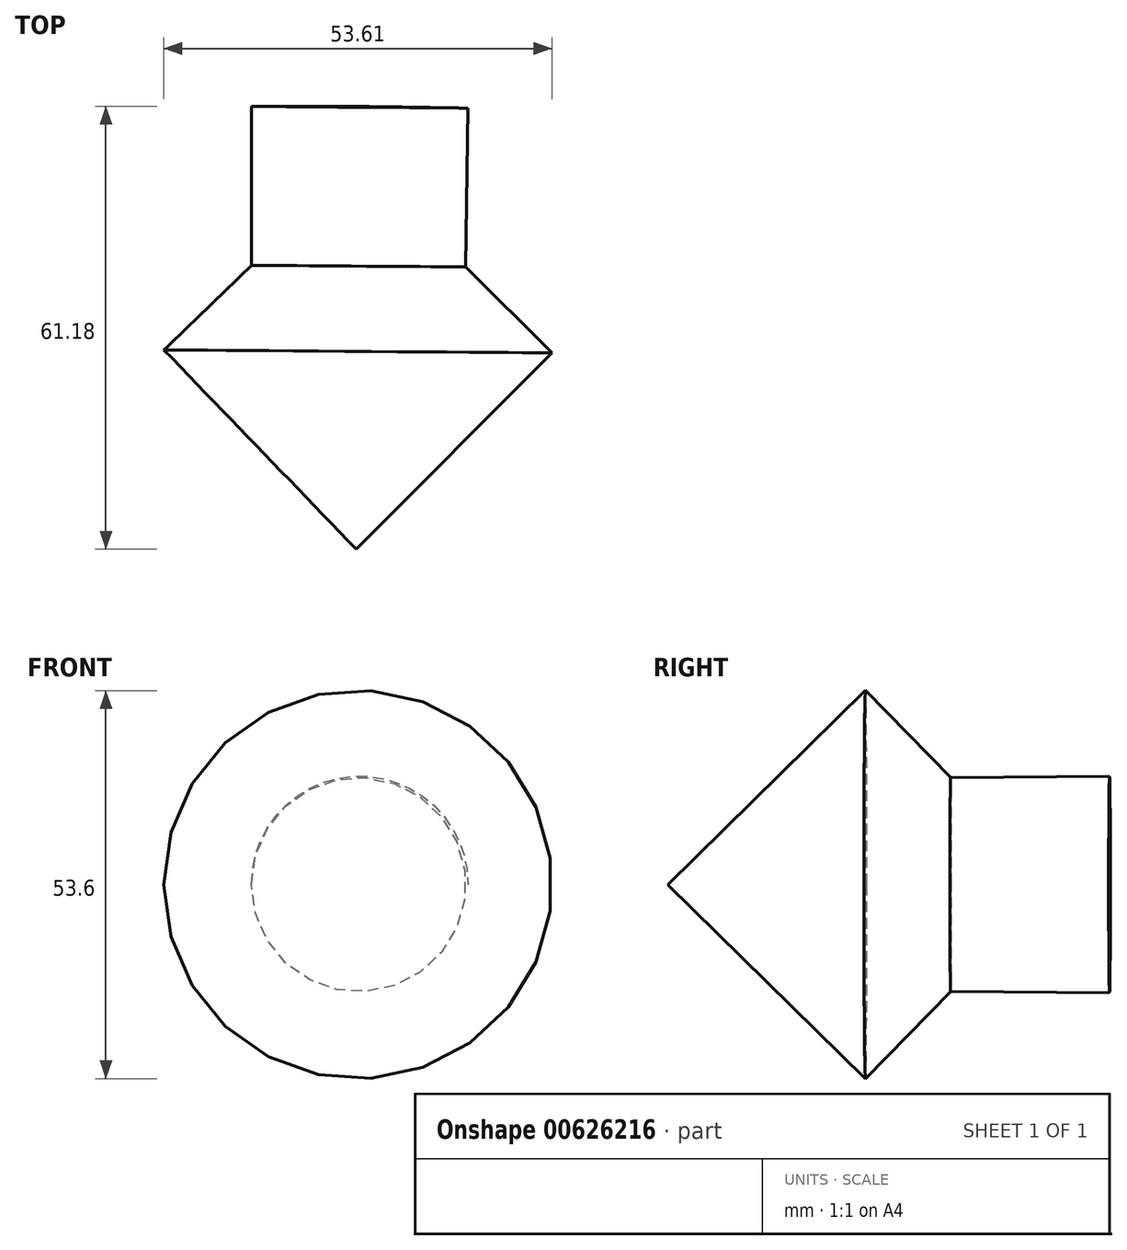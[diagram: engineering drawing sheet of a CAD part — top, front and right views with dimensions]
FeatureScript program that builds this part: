
annotation { "Feature Type Name" : "Feature", "Feature Type Description" : "" }
export const myFeature = defineFeature(function(context is Context, id is Id, definition is map)
    precondition{}
    {
        {
            var Q0;
            Q0=qCreatedBy(makeId("Top.planeOp"),FACE);
            var sketch = newSketch(context, id + "F0", { "sketchPlane" : qUnion([Q0])});
            skLineSegment(sketch, "E0.2", {"start": v(-0.48, -27.07) * mm, "end": v(-27.07, 0.48) * mm});
            skLineSegment(sketch, "E0.3", {"start": v(-27.07, 0.48) * mm, "end": v(-14.96, 12.16) * mm});
            skLineSegment(sketch, "E1.3", {"start": v(-14.96, 11.94) * mm, "end": v(-14.96, 34.1) * mm});
            skPoint(sketch, "E1.0.midPoint", {"position": v(0, 34.1) * mm});
            skPoint(sketch, "E2.orphan", {"position": v(0.48, 27.07) * mm});
            skPoint(sketch, "E3.orphan", {"position": v(-14.96, 4.18) * mm});
            skLineSegment(sketch, "E4", {"start": v(0, 34.1) * mm, "end": v(-0.48, -27.07) * mm});
            skLineSegment(sketch, "E5", {"start": v(-14.96, 34.1) * mm, "end": v(0, 34.1) * mm});
            skSolve(sketch);
        }
        {
            var Q0;
            Q0 = qSketchRegion(id + "F0", true);
            var Q1;
            Q1=sQuery(id+"F0.wireOp",EDGE,"E4");
            revolve(context, id + "F1", {"entities" : qUnion([Q0]), "axis" : qUnion([Q1]), "revolveType" : RevolveType.FULL});
        }
    });
